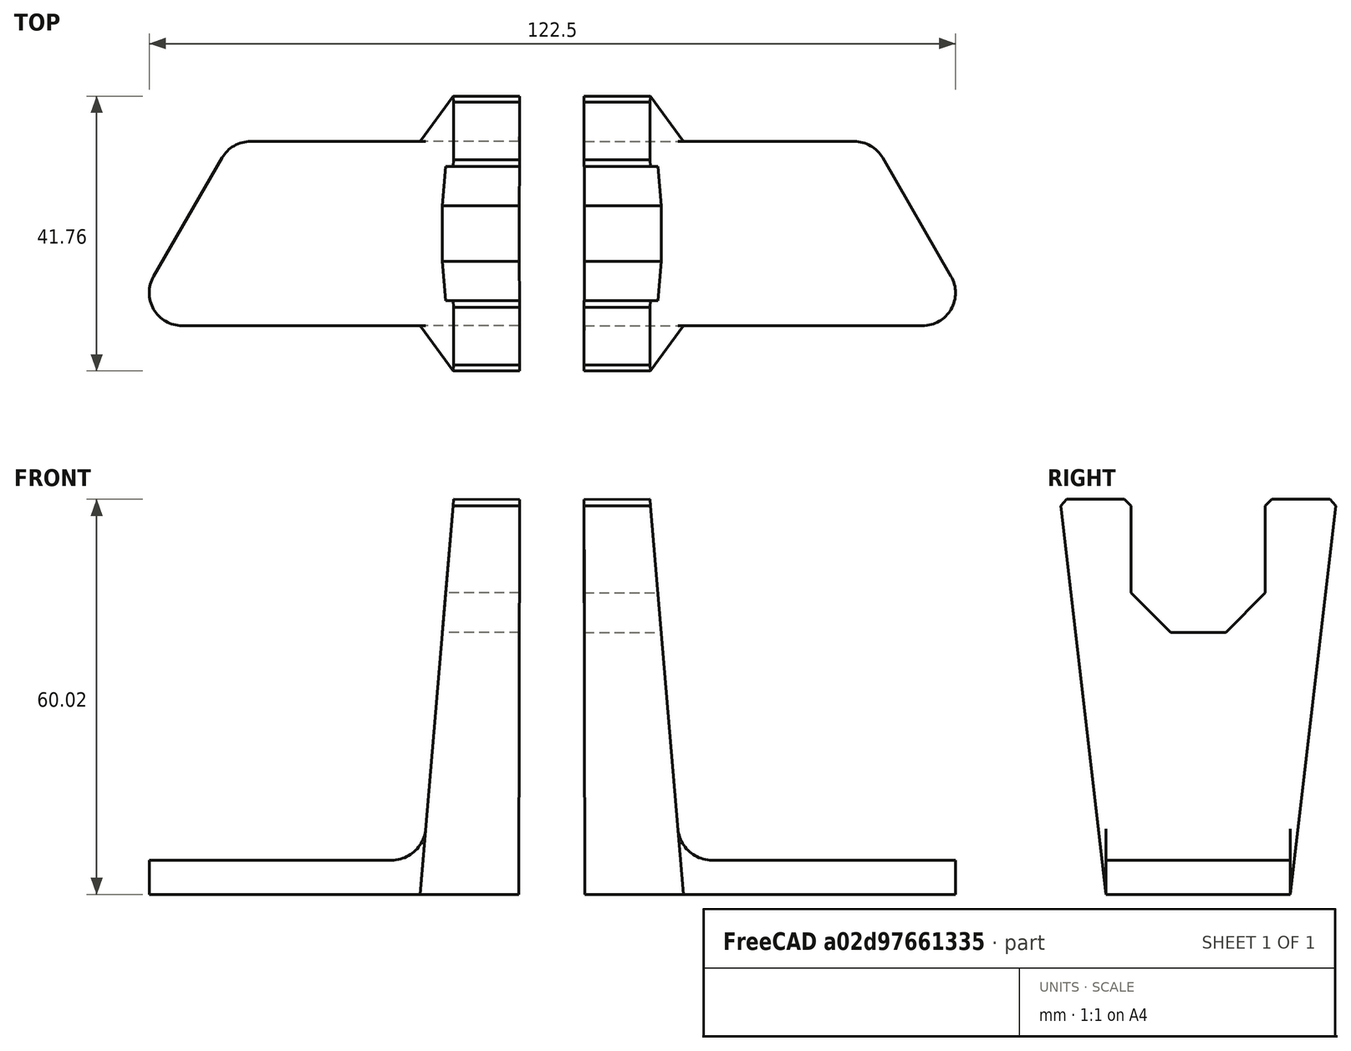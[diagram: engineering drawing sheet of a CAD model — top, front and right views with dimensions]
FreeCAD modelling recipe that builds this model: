
FCSTD DOCUMENT  (FreeCAD 0.14R3703 (Git))
Label: GOUM_Roller_Holder2
License: CC-BY 3.0
LicenseURL: http://creativecommons.org/licenses/by/3.0/
objects: Part::Box×4, Part::Fillet×4, Part::Chamfer×3, Part::Cut×3, Part::Wedge×1, Part::MultiFuse×1
note: 16 computed .brp shape members not serialized (recipe doc carries the construction recipe); baked Part::Feature solids carry a one-line shape summary decoded from their .brp

FEATURE [Part::Box] Box  label="Cube"
  Height = 5.2
  Length = 60
  Width = 28
FEATURE [Part::Wedge] Wedge
  Placement = pos=(0,0,0) rot=(0.577012,0.577012,0.578027;2.09338rad)
  X2max = 35
  X2min = -7
  Xmax = 28
  Xmin = 0
  Ymax = 60
  Ymin = 0
  Z2max = 10
  Z2min = 0
  Zmax = 15
  Zmin = 0
FEATURE [Part::Box] Box001  label="Cube001"
  Height = 20.4
  Length = 20.4
  Placement = pos=(-0.2,3.8,39.8) rot=(0,0,1;0rad)
  Width = 20.4
FEATURE [Part::Chamfer] Chamfer
  Base = -> Box001
  Edges = 2 edges r=6: [Edge9,Edge11]
FEATURE [Part::MultiFuse] Fusion
  Shapes = -> [Box,Wedge]
FEATURE [Part::Cut] Cut
  Base = -> Fusion
  Tool = -> Chamfer
FEATURE [Part::Chamfer] Chamfer001
  Base = -> Cut
  Edges = 4 edges r=1: [Edge25,Edge31,Edge40,Edge43]
FEATURE [Part::Fillet] Fillet  label="Basic holder right"
  Base = -> Chamfer001
  Edges = 1 edges r=5.2: [Edge5]
FEATURE [Part::Chamfer] Chamfer002
  Base = -> Cut
  Edges = 4 edges r=1: [Edge25,Edge31,Edge40,Edge43]
FEATURE [Part::Fillet] Fillet001  label="Basic holder left"
  Base = -> Chamfer002
  Edges = 1 edges r=5.2: [Edge5]
  Placement = pos=(-10,28,0) rot=(0,0,1;3.14159rad)
FEATURE [Part::Box] Box002  label="Cube002"
  Height = 6
  Length = 35
  Placement = pos=(60,0,0) rot=(0,0,1;0.523599rad)
  Width = 35
FEATURE [Part::Box] Box003  label="Cube003"
  Height = 6
  Length = 35
  Placement = pos=(-101,16,0) rot=(0,0,-1;0.523599rad)
  Width = 35
FEATURE [Part::Cut] Cut001
  Base = -> Fillet
  Tool = -> Box002
FEATURE [Part::Cut] Cut002
  Base = -> Fillet001
  Tool = -> Box003
FEATURE [Part::Fillet] Fillet002  label="Holder-left"
  Base = -> Cut001
  Edges = 2 edges r=5: [Edge22,Edge31]
FEATURE [Part::Fillet] Fillet003  label="Holder-right"
  Base = -> Cut002
  Edges = 2 edges r=5: [Edge23,Edge31]
